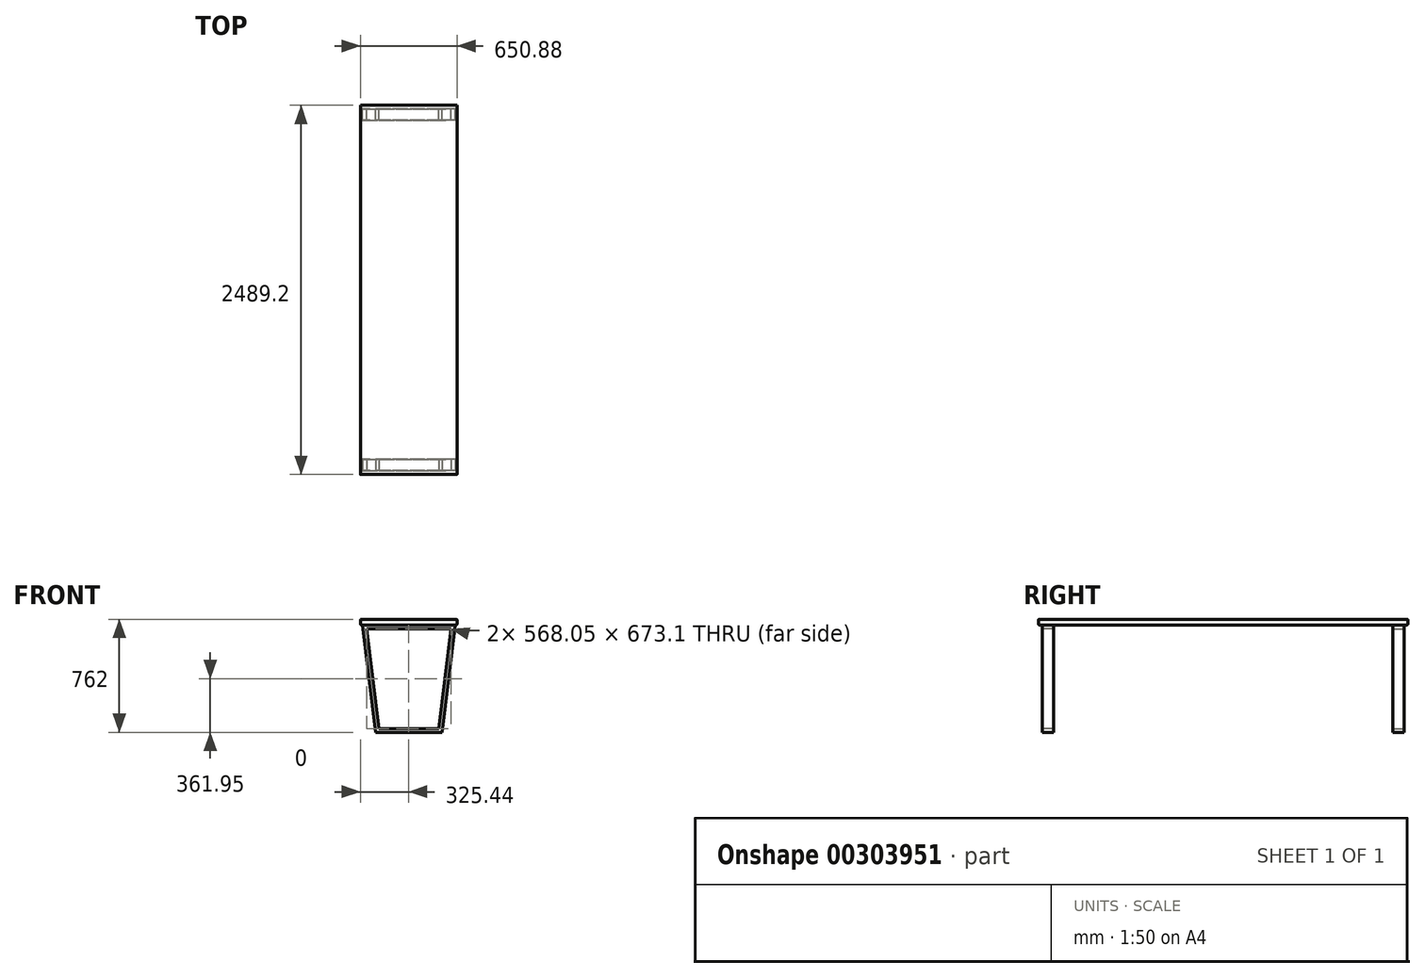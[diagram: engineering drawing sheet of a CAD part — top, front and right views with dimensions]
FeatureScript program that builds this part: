
annotation { "Feature Type Name" : "Feature", "Feature Type Description" : "" }
export const myFeature = defineFeature(function(context is Context, id is Id, definition is map)
    precondition{}
    {
        {
            var Q0;
            Q0=qCreatedBy(makeId("Front.planeOp"),FACE);
            var sketch = newSketch(context, id + "F0", { "sketchPlane" : qUnion([Q0])});
            skLineSegment(sketch, "E0.bottom", {"start": v(325.44, -19.05) * mm, "end": v(-325.44, -19.05) * mm});
            skLineSegment(sketch, "E0.top", {"start": v(325.44, 19.05) * mm, "end": v(-325.44, 19.05) * mm});
            skLineSegment(sketch, "E0.left", {"start": v(325.44, -19.05) * mm, "end": v(325.44, 19.05) * mm});
            skLineSegment(sketch, "E0.right", {"start": v(-325.44, -19.05) * mm, "end": v(-325.44, 19.05) * mm});
            skPoint(sketch, "E0.middle", {"position": v(0, 0) * mm});
            skSolve(sketch);
        }
        {
            var Q0;
            Q0 = qSketchRegion(id + "F0", true);
            extrude(context, id + "F1", {"entities" : qUnion([Q0]), "endBound" : BoundingType.SYMMETRIC, "depth" : 2489.2 * mm});
        }
        {
            var Q0;
            Q0=makeQuery(id+"F1.opExtrude","SWEPT_FACE",FACE,{"disambiguationData":[OSD([sQuery(id+"F0.wireOp",EDGE,"E0.top")])]});
            var Q1;
            Q1=makeQuery(id+"F1.opExtrude","SWEPT_FACE",FACE,{"disambiguationData":[OSD([sQuery(id+"F0.wireOp",EDGE,"E0.bottom")])]});
            fillet(context, id + "F2", {"entities" : qUnion([Q0, Q1]), "radius" : 5.08 * mm, "tangentPropagation" : true, "allowEdgeOverflow" : false});
        }
        {
            var Q0;
            Q0=makeQuery(id+"F1.opExtrude","CAP_FACE",FACE,{"disambiguationData":[OSD([sQuery(id+"F0.wireOp",EDGE,"E0.bottom"),sQuery(id+"F0.wireOp",EDGE,"E0.top"),sQuery(id+"F0.wireOp",EDGE,"E0.left"),sQuery(id+"F0.wireOp",EDGE,"E0.right")])],"isStart":true});
            cPlane(context, id + "F3", {"entities" : qUnion([Q0]), "cplaneType" : CPlaneType.OFFSET, "offset" : 25.4 * mm, "oppositeDirection" : true, "width" : 152.4 * mm, "height" : 152.4 * mm});
        }
        {
            var Q0;
            Q0=qCreatedBy(id+"F3.planeOp",FACE);
            var sketch = newSketch(context, id + "F4", { "sketchPlane" : qUnion([Q0])});
            skLineSegment(sketch, "E1", {"start": v(0, 229.5) * mm, "end": v(0, -712.06) * mm, "construction": true});
            skLineSegment(sketch, "E2", {"start": v(0, -19.05) * mm, "end": v(312.74, -19.05) * mm});
            skLineSegment(sketch, "E3", {"start": v(312.74, -19.05) * mm, "end": v(223.84, -742.95) * mm});
            skLineSegment(sketch, "E4", {"start": v(223.84, -742.95) * mm, "end": v(0, -742.95) * mm});
            skLineSegment(sketch, "E5.MirrorCS", {"start": v(-312.74, -19.05) * mm, "end": v(-223.84, -742.95) * mm});
            skLineSegment(sketch, "E6.MirrorCS", {"start": v(0, -19.05) * mm, "end": v(-312.74, -19.05) * mm});
            skLineSegment(sketch, "E7.MirrorCS", {"start": v(-223.84, -742.95) * mm, "end": v(0, -742.95) * mm});
            skLineSegment(sketch, "E8.0", {"start": v(0, -44.45) * mm, "end": v(284.03, -44.45) * mm});
            skLineSegment(sketch, "E8.1", {"start": v(-284.03, -44.45) * mm, "end": v(-201.37, -717.55) * mm});
            skLineSegment(sketch, "E8.2", {"start": v(-201.37, -717.55) * mm, "end": v(0, -717.55) * mm});
            skLineSegment(sketch, "E8.3", {"start": v(0, -44.45) * mm, "end": v(-284.03, -44.45) * mm});
            skLineSegment(sketch, "E8.4", {"start": v(201.37, -717.55) * mm, "end": v(0, -717.55) * mm});
            skLineSegment(sketch, "E8.5", {"start": v(284.03, -44.45) * mm, "end": v(201.37, -717.55) * mm});
            skSolve(sketch);
        }
        {
            var Q0;
            Q0 = qSketchRegion(id + "F4", true);
            extrude(context, id + "F5", {"entities" : qUnion([Q0]), "oppositeDirection" : true, "depth" : 76.2 * mm});
        }
        {
            var Q0;
            Q0=makeQuery(id+"F5.opExtrude","SWEPT_BODY",BODY,{"disambiguationData":[OSD([sQuery(id+"F4.wireOp",EDGE,"E2"),sQuery(id+"F4.wireOp",EDGE,"E3"),sQuery(id+"F4.wireOp",EDGE,"E4"),sQuery(id+"F4.wireOp",EDGE,"E5.MirrorCS"),sQuery(id+"F4.wireOp",EDGE,"E6.MirrorCS"),sQuery(id+"F4.wireOp",EDGE,"E7.MirrorCS"),sQuery(id+"F4.wireOp",EDGE,"E8.0"),sQuery(id+"F4.wireOp",EDGE,"E8.1"),sQuery(id+"F4.wireOp",EDGE,"E8.2"),sQuery(id+"F4.wireOp",EDGE,"E8.3"),sQuery(id+"F4.wireOp",EDGE,"E8.4"),sQuery(id+"F4.wireOp",EDGE,"E8.5")])]});
            var Q1;
            Q1=qCreatedBy(makeId("Front.planeOp"),FACE);
            mirror(context, id + "F6", {"entities" : qUnion([Q0]), "mirrorPlane" : qUnion([Q1])});
        }
    });
